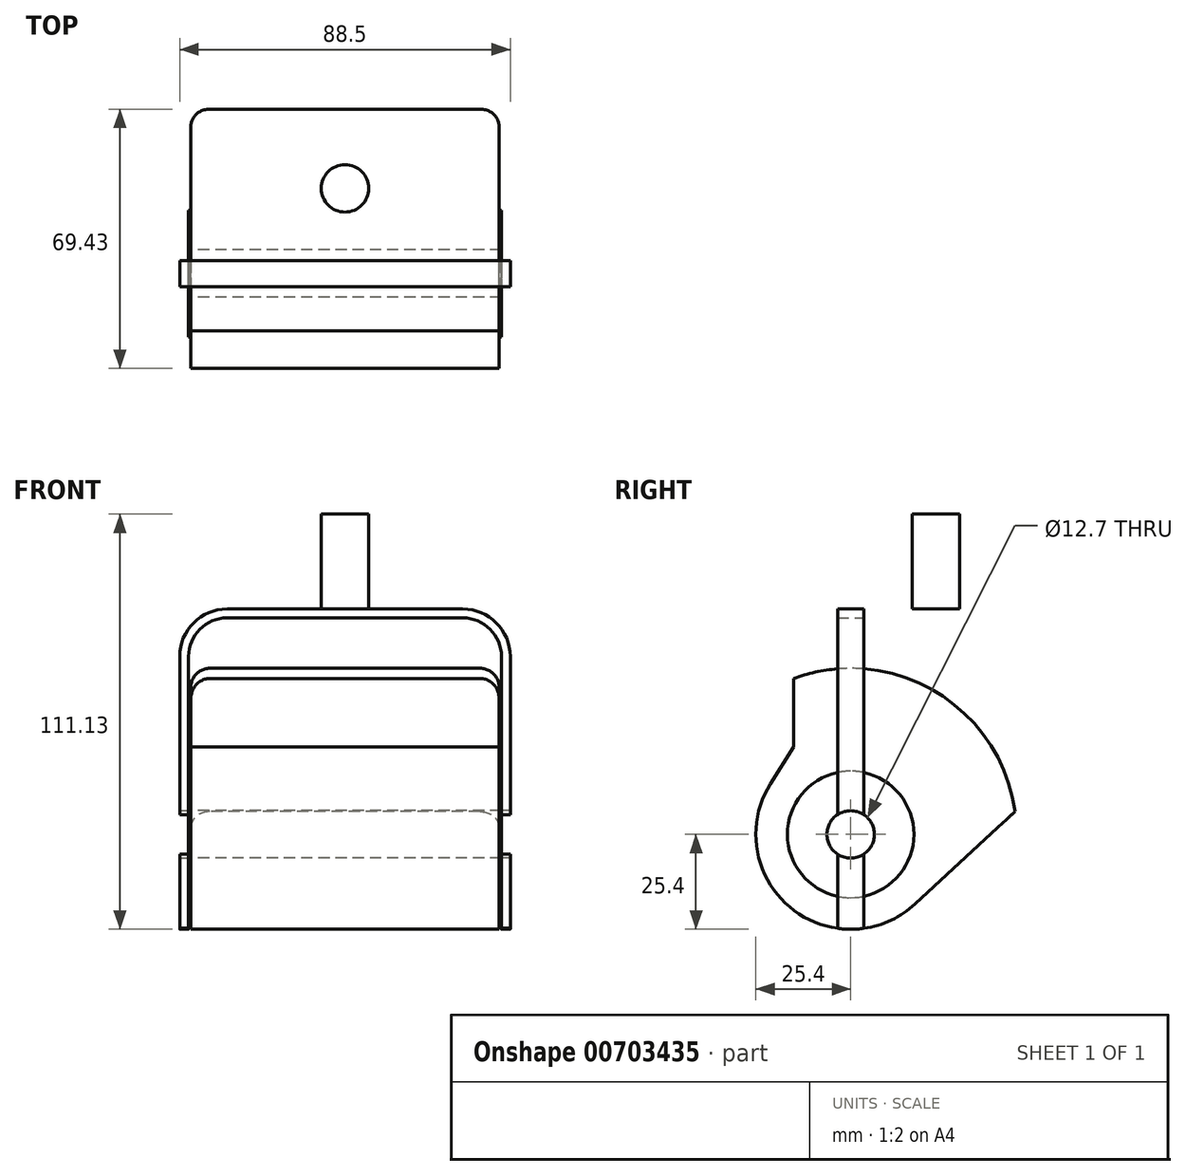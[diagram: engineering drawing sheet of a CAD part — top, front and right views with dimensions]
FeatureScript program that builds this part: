
annotation { "Feature Type Name" : "Feature", "Feature Type Description" : "" }
export const myFeature = defineFeature(function(context is Context, id is Id, definition is map)
    precondition{}
    {
        {
            assignVariable(context, id + "F0", {"name" : "mnt_hgt", "anyValue" : 4.12});
        }
        {
            assignVariable(context, id + "F1", {"name" : "wheel_dia", "anyValue" : 3.5});
        }
        {
            var Q0;
            Q0=qCreatedBy(makeId("Top.planeOp"),FACE);
            cPlane(context, id + "F2", {"entities" : qUnion([Q0]), "cplaneType" : CPlaneType.OFFSET, "offset" : (getVariable(context, 'mnt_hgt')) * mm, "width" : 152.4 * mm, "height" : 152.4 * mm});
        }
        {
            var Q0;
            Q0=qCreatedBy(makeId("Front.planeOp"),FACE);
            var sketch = newSketch(context, id + "F3", { "sketchPlane" : qUnion([Q0])});
            skLineSegment(sketch, "E0.bottom", {"start": v(0, 0) * mm, "end": v(41.28, 0) * mm});
            skLineSegment(sketch, "E0.top", {"start": v(0, 27.52) * mm, "end": v(41.28, 27.52) * mm});
            skLineSegment(sketch, "E0.right", {"start": v(41.28, 0) * mm, "end": v(41.28, 27.52) * mm});
            skLineSegment(sketch, "E1", {"start": v(-71.3, 44.45) * mm, "end": v(68.12, 44.45) * mm, "construction": true});
            skLineSegment(sketch, "E2.bottom", {"start": v(0, 38.1) * mm, "end": v(41.87, 38.1) * mm});
            skLineSegment(sketch, "E2.right", {"start": v(41.87, 38.1) * mm, "end": v(41.87, 27.52) * mm});
            skPoint(sketch, "E3", {"position": v(0, 27.52) * mm});
            skLineSegment(sketch, "E4", {"start": v(0, 0) * mm, "end": v(0, 38.1) * mm});
            skLineSegment(sketch, "E5.trimOffspring", {"start": v(0, 27.52) * mm, "end": v(41.87, 27.52) * mm});
            skLineSegment(sketch, "E6", {"start": v(0, 112.14) * mm, "end": v(0, 93.39) * mm, "construction": true});
            skSolve(sketch);
        }
        {
            var Q0;
            Q0=makeQuery(id+"F3.imprint","IMPRINT",FACE,{"disambiguationData":[TD([[makeQuery(id+"F3.imprint","IMPRINT",EDGE,{"derivedFrom":sQuery(id+"F3.wireOp",EDGE,"E2.bottom")}),-1.0]])]});
            var Q1;
            Q1=makeQuery(id+"F3.imprint","IMPRINT",FACE,{"disambiguationData":[TD([[makeQuery(id+"F3.imprint","IMPRINT",EDGE,{"derivedFrom":sQuery(id+"F3.wireOp",EDGE,"E0.bottom")}),1.0]])]});
            var Q2;
            Q2=sQuery(id+"F3.wireOp",EDGE,"E1");
            revolve(context, id + "F4", {"surfaceOperationType" : NewSurfaceOperationType.NEW, "entities" : qUnion([Q0, Q1]), "axis" : qUnion([Q2]), "revolveType" : RevolveType.FULL});
        }
        {
            var Q0;
            Q0=makeQuery(id+"F4.opRevolve","SWEPT_EDGE",EDGE,{"disambiguationData":[OSD([sQuery(id+"F3.wireOp",EDGE,"E0.bottom"),sQuery(id+"F3.wireOp",EDGE,"E0.right")])]});
            fillet(context, id + "F5", {"entities" : qUnion([Q0]), "radius" : 5.08 * mm, "tangentPropagation" : true, "allowEdgeOverflow" : false});
        }
        {
            var Q0;
            Q0=qCreatedBy(makeId("Front.planeOp"),FACE);
            var sketch = newSketch(context, id + "F6", { "sketchPlane" : qUnion([Q0])});
            skLineSegment(sketch, "E7", {"start": v(0, 104.78) * mm, "end": v(31.55, 104.78) * mm});
            skLineSegment(sketch, "E8", {"start": v(44.25, 92.08) * mm, "end": v(44.25, 19.05) * mm});
            skPoint(sketch, "E9.visualSharp", {"position": v(44.25, 104.78) * mm});
            skArc(sketch, "E9.filletArc", {"start": v(44.25, 92.08) * mm, "mid": v(40.53, 101.06) * mm, "end": v(31.55, 104.78) * mm});
            skLineSegment(sketch, "E10.0", {"start": v(41.9, 92.08) * mm, "end": v(41.9, 19.05) * mm});
            skArc(sketch, "E10.1", {"start": v(41.9, 92.08) * mm, "mid": v(38.86, 99.38) * mm, "end": v(31.55, 102.41) * mm});
            skLineSegment(sketch, "E10.2", {"start": v(0, 102.41) * mm, "end": v(31.55, 102.41) * mm});
            skLineSegment(sketch, "E11", {"start": v(0, 104.78) * mm, "end": v(0, 102.41) * mm});
            skLineSegment(sketch, "E12", {"start": v(41.9, 19.05) * mm, "end": v(44.25, 19.05) * mm});
            skSolve(sketch);
        }
        {
            var Q0;
            Q0 = qSketchRegion(id + "F6", true);
            extrude(context, id + "F7", {"entities" : qUnion([Q0]), "endBound" : BoundingType.SYMMETRIC, "depth" : (2 * getVariable(context, 'wheel_dia')) * mm, "offsetDistance" : 25.4 * mm});
        }
        {
            var Q0;
            Q0=qCreatedBy(makeId("Right.planeOp"),FACE);
            var sketch = newSketch(context, id + "F8", { "sketchPlane" : qUnion([Q0])});
            skLineSegment(sketch, "E13", {"start": v(-15.3, 104.78) * mm, "end": v(-15.3, 67.82) * mm});
            skLineSegment(sketch, "E14", {"start": v(-15.3, 67.82) * mm, "end": v(-21.49, 58) * mm});
            skLineSegment(sketch, "E15", {"start": v(-46.04, 19.05) * mm, "end": v(9.95, 19.05) * mm, "construction": true});
            skLineSegment(sketch, "E16", {"start": v(9.95, 19.05) * mm, "end": v(17.25, 25.8) * mm, "construction": true});
            skLineSegment(sketch, "E17", {"start": v(60.9, 66.19) * mm, "end": v(60.9, 104.78) * mm});
            skLineSegment(sketch, "E18", {"start": v(60.9, 104.78) * mm, "end": v(-15.3, 104.78) * mm});
            skPoint(sketch, "E19", {"position": v(-18.05, 19.05) * mm});
            skCircle(sketch, "E20.0", {"center": v(0, 44.45) * mm, "radius": 6.35 * mm});
            skArc(sketch, "E21", {"start": v(-21.49, 58) * mm, "mid": v(-16.24, 24.92) * mm, "end": v(17.25, 25.8) * mm});
            skArc(sketch, "E22", {"start": v(17.25, 25.8) * mm, "mid": v(16.24, 63.98) * mm, "end": v(-21.49, 58) * mm, "construction": true});
            skLineSegment(sketch, "E23", {"start": v(-21.49, 58) * mm, "end": v(-46.04, 19.05) * mm, "construction": true});
            skLineSegment(sketch, "E24", {"start": v(17.25, 25.8) * mm, "end": v(60.9, 66.19) * mm});
            skSolve(sketch);
        }
        {
            var Q0;
            Q0 = qSketchRegion(id + "F8", true);
            extrude(context, id + "F9", {"entities" : qUnion([Q0]), "operationType" : NewBodyOperationType.INTERSECT, "endBound" : BoundingType.THROUGH_ALL, "depth" : 25.4 * mm, "offsetDistance" : 25.4 * mm});
        }
        {
            var Q0;
            Q0=makeQuery(id+"F4.opRevolve","SWEPT_BODY",BODY,{"disambiguationData":[OSD([sQuery(id+"F3.wireOp",EDGE,"E0.bottom"),sQuery(id+"F3.wireOp",EDGE,"E0.right"),sQuery(id+"F3.wireOp",EDGE,"E2.bottom"),sQuery(id+"F3.wireOp",EDGE,"E2.right"),sQuery(id+"F3.wireOp",EDGE,"E4"),sQuery(id+"F3.wireOp",EDGE,"E5.trimOffspring")])]});
            var Q1;
            Q1=makeQuery(id+"F7.opExtrude","SWEPT_BODY",BODY,{"disambiguationData":[OSD([sQuery(id+"F6.wireOp",EDGE,"E7"),sQuery(id+"F6.wireOp",EDGE,"E8"),sQuery(id+"F6.wireOp",EDGE,"E9.filletArc"),sQuery(id+"F6.wireOp",EDGE,"E10.0"),sQuery(id+"F6.wireOp",EDGE,"E10.1"),sQuery(id+"F6.wireOp",EDGE,"E10.2"),sQuery(id+"F6.wireOp",EDGE,"E11"),sQuery(id+"F6.wireOp",EDGE,"E12")])]});
            var Q2;
            Q2=qCreatedBy(makeId("Right.planeOp"),FACE);
            mirror(context, id + "F10", {"operationType" : NewBodyOperationType.ADD, "entities" : qUnion([Q0, Q1]), "mirrorPlane" : qUnion([Q2])});
        }
        {
            var Q0;
            {var subQ0=makeQuery(id+"F7.opExtrude","SWEPT_FACE",FACE,{"disambiguationData":[OSD([sQuery(id+"F6.wireOp",EDGE,"E7")])]});Q0=makeQuery(id+"F10.boolean.opBoolean","MERGE",FACE,{"derivedFrom":[subQ0,makeQuery(id+"F10.opPattern","COPY",FACE,{"derivedFrom":subQ0,"instanceName":"1"})]});}
            var sketch = newSketch(context, id + "F11", { "sketchPlane" : qUnion([Q0])});
            skCircle(sketch, "E25", {"center": v(0, 22.8) * mm, "radius": 6.35 * mm});
            skSolve(sketch);
        }
        {
            var Q0;
            Q0 = qSketchRegion(id + "F11", true);
            extrude(context, id + "F12", {"entities" : qUnion([Q0]), "operationType" : NewBodyOperationType.ADD, "depth" : 25.4 * mm, "offsetDistance" : 25.4 * mm});
        }
    });
